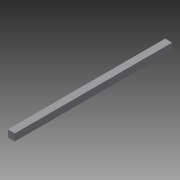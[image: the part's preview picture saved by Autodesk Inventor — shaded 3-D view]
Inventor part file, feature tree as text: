
AUTODESK INVENTOR PART (.ipt)
format: ipt  version: 2015 (Build 190159000, 159)  size: 69,120 bytes
history: native  units: in
note: dims shown in document units (in); Inventor stores cm internally (conversion verified against a paired STEP export)
features: extrude x1, sketch x1
ambient origin geometry x8: Origin, YZ Plane, XZ Plane, XY Plane, X Axis, Y Axis, Z Axis, Center Point
bodies: Solid1 (feature_tree)
feature tree (2):
  extrude  "Extrusion1"  Depth=0.75in
  sketch  "Sketch1"  dims[d0=0.75in d1=0.75in d2=17.0in d3=0.0in]
